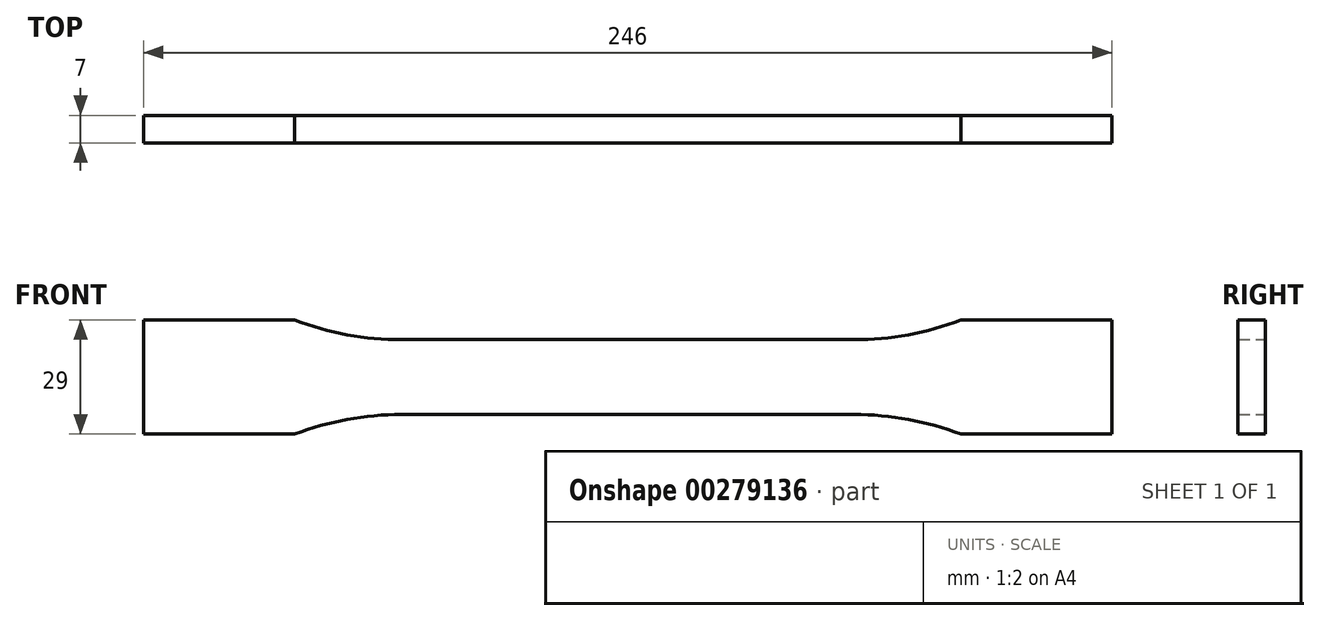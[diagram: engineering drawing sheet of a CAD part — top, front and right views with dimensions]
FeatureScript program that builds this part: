
annotation { "Feature Type Name" : "Feature", "Feature Type Description" : "" }
export const myFeature = defineFeature(function(context is Context, id is Id, definition is map)
    precondition{}
    {
        {
            var Q0;
            Q0=qCreatedBy(makeId("Front.planeOp"),FACE);
            var sketch = newSketch(context, id + "F0", { "sketchPlane" : qUnion([Q0])});
            skLineSegment(sketch, "E0", {"start": v(0, 9.5) * mm, "end": v(57.5, 9.5) * mm});
            skArc(sketch, "E1", {"start": v(57.5, 9.5) * mm, "mid": v(71.28, 10.76) * mm, "end": v(84.61, 14.5) * mm});
            skLineSegment(sketch, "E2", {"start": v(84.61, 14.5) * mm, "end": v(123, 14.5) * mm});
            skLineSegment(sketch, "E3.MirrorCS", {"start": v(84.61, -14.5) * mm, "end": v(123, -14.5) * mm});
            skLineSegment(sketch, "E4.MirrorCS", {"start": v(0, -9.5) * mm, "end": v(57.5, -9.5) * mm});
            skArc(sketch, "E5.MirrorCS", {"start": v(57.5, -9.5) * mm, "mid": v(71.28, -10.76) * mm, "end": v(84.61, -14.5) * mm});
            skArc(sketch, "E6.MirrorCS", {"start": v(-57.5, -9.5) * mm, "mid": v(-71.28, -10.76) * mm, "end": v(-84.61, -14.5) * mm});
            skLineSegment(sketch, "E7.MirrorCS", {"start": v(0, -9.5) * mm, "end": v(-57.5, -9.5) * mm});
            skLineSegment(sketch, "E8.MirrorCS", {"start": v(0, 9.5) * mm, "end": v(-57.5, 9.5) * mm});
            skLineSegment(sketch, "E9.MirrorCS", {"start": v(-84.61, -14.5) * mm, "end": v(-123, -14.5) * mm});
            skLineSegment(sketch, "E10.MirrorCS", {"start": v(-84.61, 14.5) * mm, "end": v(-123, 14.5) * mm});
            skArc(sketch, "E11.MirrorCS", {"start": v(-57.5, 9.5) * mm, "mid": v(-71.28, 10.76) * mm, "end": v(-84.61, 14.5) * mm});
            skLineSegment(sketch, "E12", {"start": v(-123, 14.5) * mm, "end": v(-123, -14.5) * mm});
            skLineSegment(sketch, "E13", {"start": v(123, 14.5) * mm, "end": v(123, -14.5) * mm});
            skSolve(sketch);
        }
        {
            var Q0;
            Q0=makeQuery(id+"F0.imprint","IMPRINT",FACE,{"disambiguationData":[TD([[makeQuery(id+"F0.imprint","IMPRINT",EDGE,{"derivedFrom":sQuery(id+"F0.wireOp",EDGE,"E0")}),-1.0]])]});
            extrude(context, id + "F1", {"entities" : qUnion([Q0]), "endBound" : BoundingType.SYMMETRIC, "depth" : 7 * mm});
        }
    });
